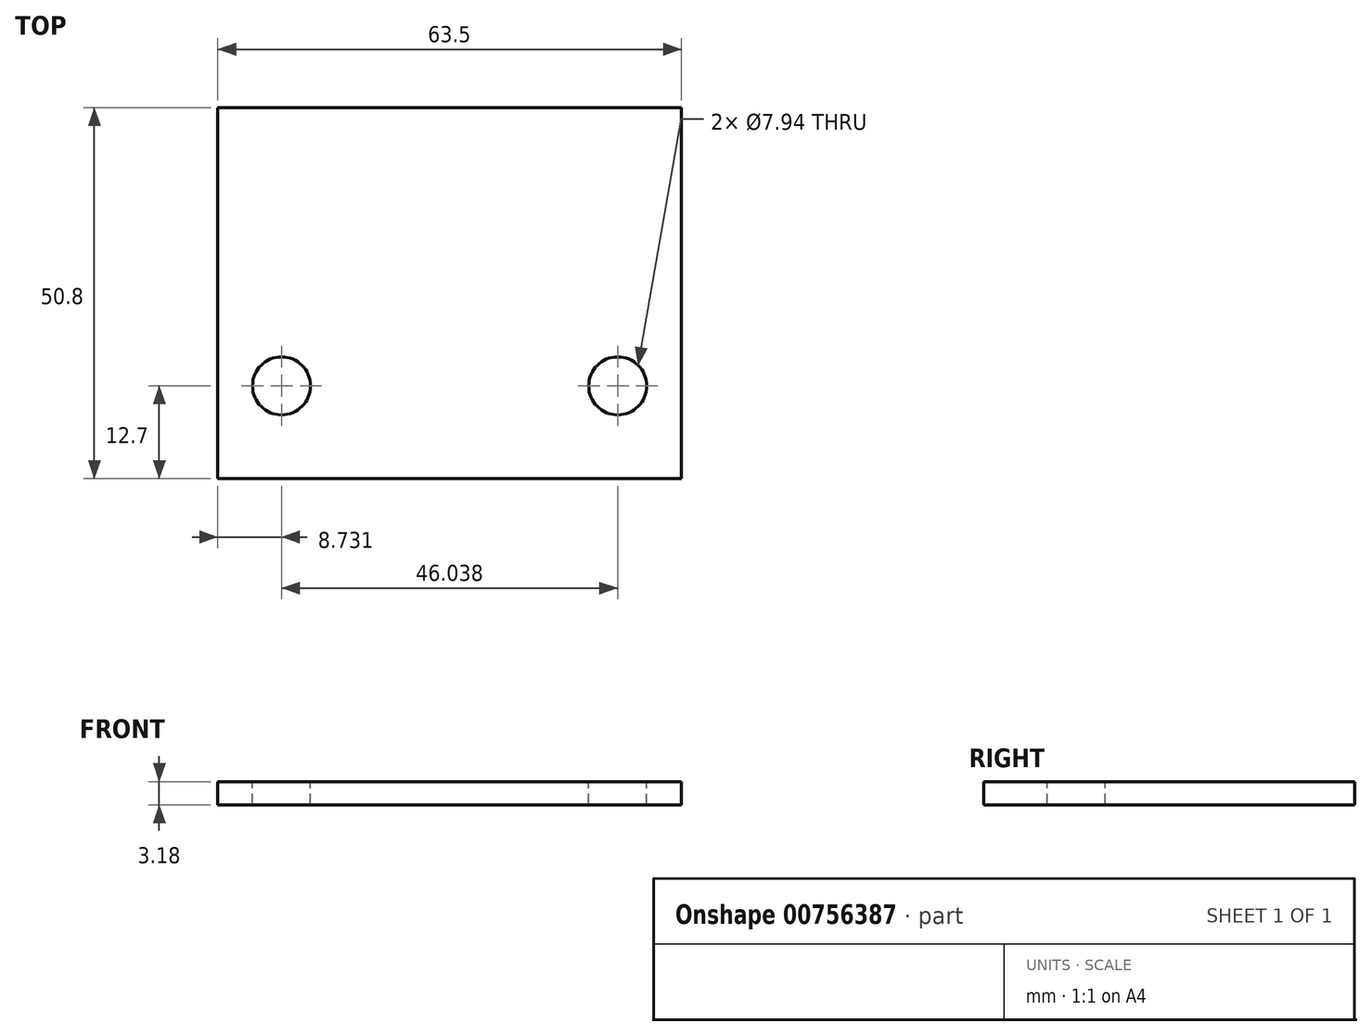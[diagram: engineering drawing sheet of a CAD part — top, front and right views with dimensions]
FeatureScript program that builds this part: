
annotation { "Feature Type Name" : "Feature", "Feature Type Description" : "" }
export const myFeature = defineFeature(function(context is Context, id is Id, definition is map)
    precondition{}
    {
        {
            var Q0;
            Q0=qCreatedBy(makeId("Front.planeOp"),FACE);
            var sketch = newSketch(context, id + "F0", { "sketchPlane" : qUnion([Q0])});
            skLineSegment(sketch, "E0.bottom", {"start": v(0, 0) * mm, "end": v(63.5, 0) * mm});
            skLineSegment(sketch, "E0.top", {"start": v(0, 3.17) * mm, "end": v(63.5, 3.17) * mm});
            skLineSegment(sketch, "E0.left", {"start": v(0, 0) * mm, "end": v(0, 3.17) * mm});
            skLineSegment(sketch, "E0.right", {"start": v(63.5, 0) * mm, "end": v(63.5, 3.18) * mm});
            skSolve(sketch);
        }
        {
            var Q0;
            Q0=makeQuery(id+"F0.imprint","IMPRINT",FACE,{"disambiguationData":[TD([[makeQuery(id+"F0.imprint","IMPRINT",EDGE,{"derivedFrom":sQuery(id+"F0.wireOp",EDGE,"E0.bottom")}),1.0]])]});
            extrude(context, id + "F1", {"entities" : qUnion([Q0]), "depth" : 50.8 * mm, "offsetDistance" : 25.4 * mm});
        }
        {
            var Q0;
            Q0=makeQuery(id+"F1.opExtrude","SWEPT_FACE",FACE,{"disambiguationData":[OSD([sQuery(id+"F0.wireOp",EDGE,"E0.top")])]});
            var sketch = newSketch(context, id + "F2", { "sketchPlane" : qUnion([Q0])});
            skLineSegment(sketch, "E1", {"start": v(31.75, -50.8) * mm, "end": v(31.75, 0) * mm, "construction": true});
            skLineSegment(sketch, "E2", {"start": v(8.73, -38.1) * mm, "end": v(54.77, -38.1) * mm, "construction": true});
            skPoint(sketch, "E3", {"position": v(31.75, -38.1) * mm});
            skCircle(sketch, "E4", {"center": v(8.73, -38.1) * mm, "radius": 3.97 * mm});
            skCircle(sketch, "E5", {"center": v(54.77, -38.1) * mm, "radius": 3.97 * mm});
            skLineSegment(sketch, "E6", {"start": v(0, -25.4) * mm, "end": v(63.5, -25.4) * mm, "construction": true});
            skSolve(sketch);
        }
        {
            var Q0;
            Q0=makeQuery(id+"F2.imprint","IMPRINT",FACE,{"disambiguationData":[TD([[makeQuery(id+"F2.imprint","IMPRINT",EDGE,{"derivedFrom":sQuery(id+"F2.wireOp",EDGE,"E4")}),1.0]])]});
            var Q1;
            Q1=makeQuery(id+"F2.imprint","IMPRINT",FACE,{"disambiguationData":[TD([[makeQuery(id+"F2.imprint","IMPRINT",EDGE,{"derivedFrom":sQuery(id+"F2.wireOp",EDGE,"E5")}),1.0]])]});
            extrude(context, id + "F3", {"entities" : qUnion([Q0, Q1]), "operationType" : NewBodyOperationType.REMOVE, "endBound" : BoundingType.THROUGH_ALL, "oppositeDirection" : true, "depth" : 25.4 * mm, "offsetDistance" : 25.4 * mm});
        }
    });
